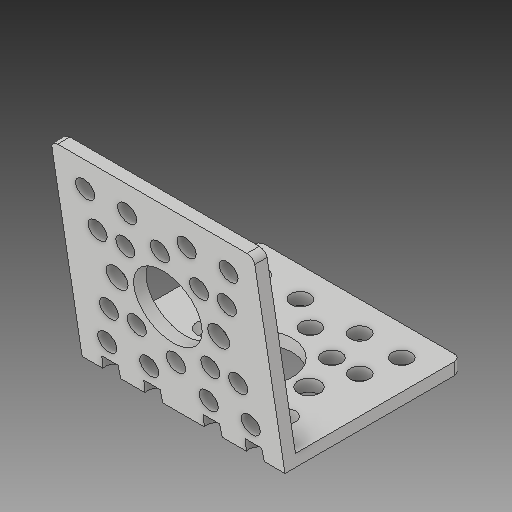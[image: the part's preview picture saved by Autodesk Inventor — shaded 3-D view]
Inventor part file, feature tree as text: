
AUTODESK INVENTOR PART (.ipt)
format: ipt  version: 2017 (Build 210142000, 142)  size: 268,800 bytes
history: native  units: in
note: dims shown in document units (in); Inventor stores cm internally (conversion verified against a paired STEP export)
features: direct_edit x1, fillet x1, revolve x1
ambient origin geometry x8: Origin, YZ Plane, XZ Plane, XY Plane, X Axis, Y Axis, Z Axis, Center Point
bodies: Solid1 (feature_tree)
feature tree (3):
  direct_edit  "Direct Edit1"
  fillet  "Fillet1"  Radius=0.0602in
  revolve  "Rotate1"  [1 undecoded]
note: 1 required parameter value undecoded (feature->parameter linkage not recoverable at this tier; creation-order binding heuristic only, values carry confidence <= 0.55)
